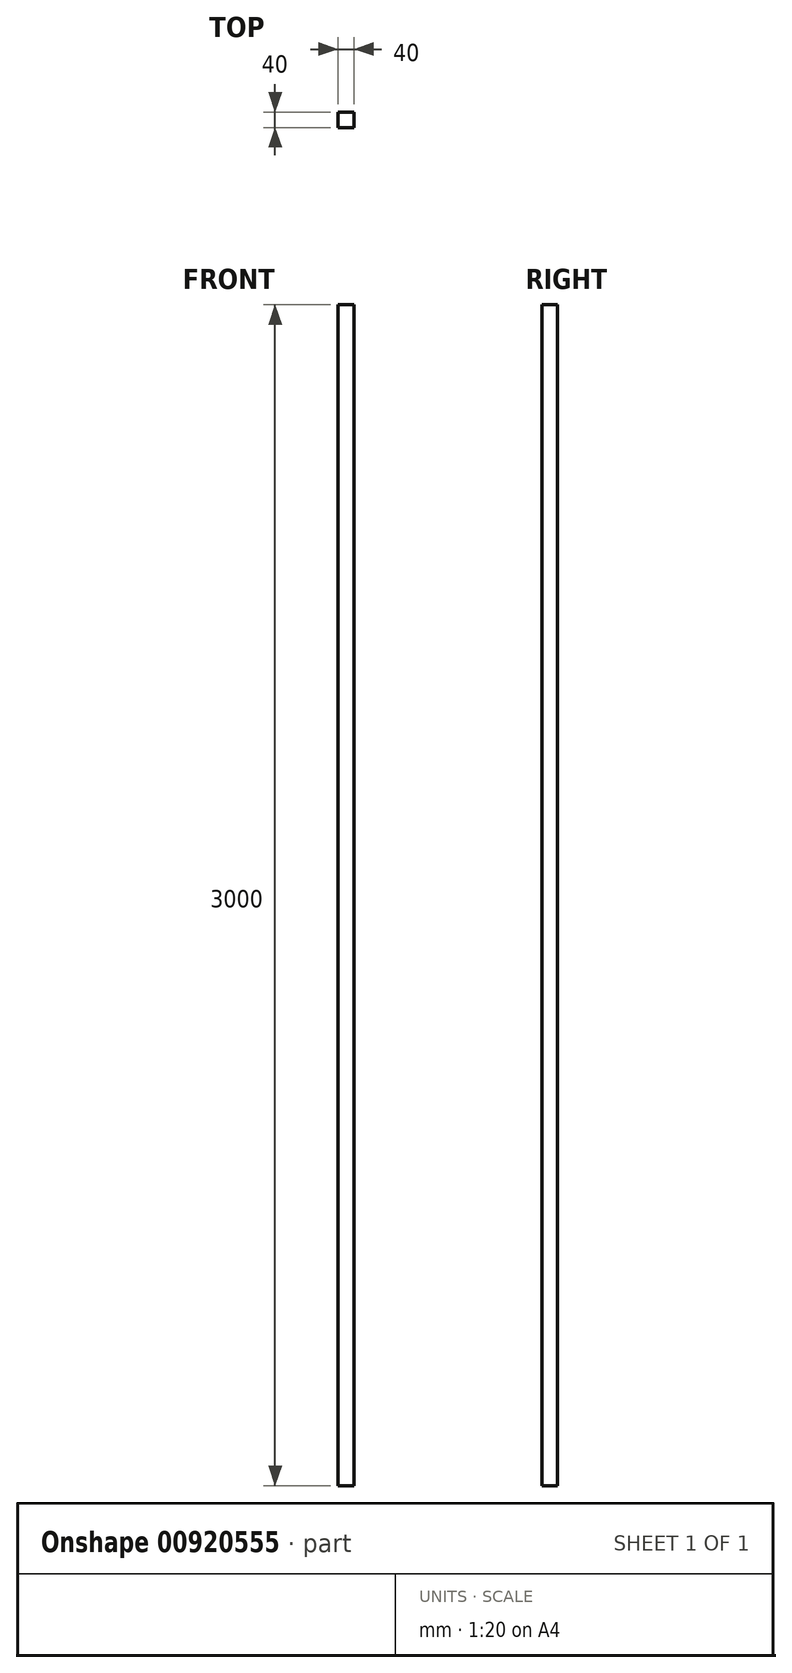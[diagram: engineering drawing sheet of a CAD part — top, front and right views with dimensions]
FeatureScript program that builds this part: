
annotation { "Feature Type Name" : "Feature", "Feature Type Description" : "" }
export const myFeature = defineFeature(function(context is Context, id is Id, definition is map)
    precondition{}
    {
        {
            var Q0;
            Q0=qCreatedBy(makeId("Top.planeOp"),FACE);
            var sketch = newSketch(context, id + "F0", { "sketchPlane" : qUnion([Q0])});
            skLineSegment(sketch, "E0.bottom", {"start": v(0, 0) * mm, "end": v(40, 0) * mm});
            skLineSegment(sketch, "E0.top", {"start": v(0, -40) * mm, "end": v(40, -40) * mm});
            skLineSegment(sketch, "E0.left", {"start": v(0, 0) * mm, "end": v(0, -40) * mm});
            skLineSegment(sketch, "E0.right", {"start": v(40, 0) * mm, "end": v(40, -40) * mm});
            skSolve(sketch);
        }
        {
            var Q0;
            Q0=makeQuery(id+"F0.imprint","IMPRINT",FACE,{"disambiguationData":[TD([[makeQuery(id+"F0.imprint","IMPRINT",EDGE,{"derivedFrom":sQuery(id+"F0.wireOp",EDGE,"E0.bottom")}),-1.0]])]});
            extrude(context, id + "F1", {"entities" : qUnion([Q0]), "depth" : 3000 * mm, "offsetDistance" : 25 * mm});
        }
    });
